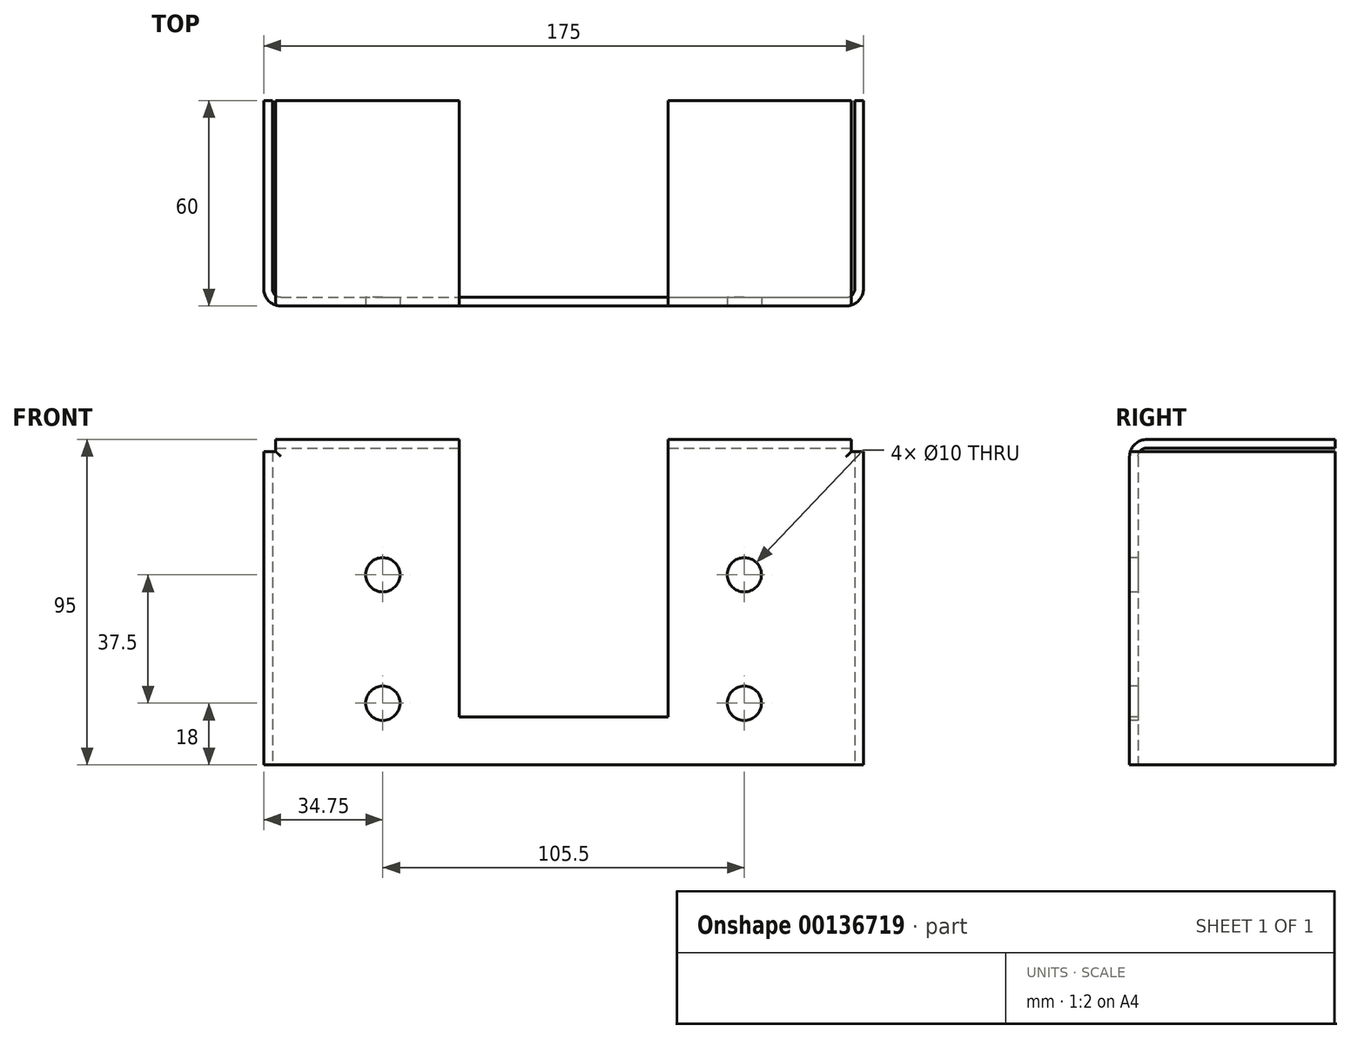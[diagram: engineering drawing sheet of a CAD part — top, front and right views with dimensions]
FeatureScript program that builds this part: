
annotation { "Feature Type Name" : "Feature", "Feature Type Description" : "" }
export const myFeature = defineFeature(function(context is Context, id is Id, definition is map)
    precondition{}
    {
        {
            var Q0;
            Q0=qCreatedBy(makeId("Top.planeOp"),FACE);
            var sketch = newSketch(context, id + "F0", { "sketchPlane" : qUnion([Q0])});
            skLineSegment(sketch, "E0.bottom", {"start": v(-87.5, -30) * mm, "end": v(87.5, -30) * mm});
            skLineSegment(sketch, "E0.top", {"start": v(-87.5, 30) * mm, "end": v(87.5, 30) * mm});
            skLineSegment(sketch, "E0.left", {"start": v(-87.5, -30) * mm, "end": v(-87.5, 30) * mm});
            skLineSegment(sketch, "E0.right", {"start": v(87.5, -30) * mm, "end": v(87.5, 30) * mm});
            skPoint(sketch, "E0.middle", {"position": v(0, 0) * mm});
            skSolve(sketch);
        }
        {
            var Q0;
            Q0 = qSketchRegion(id + "F0", true);
            extrude(context, id + "F1", {"entities" : qUnion([Q0]), "depth" : 95 * mm});
        }
        {
            var Q0;
            Q0=makeQuery(id+"F1.opExtrude","SWEPT_FACE",FACE,{"disambiguationData":[OSD([sQuery(id+"F0.wireOp",EDGE,"E0.bottom")])]});
            var sketch = newSketch(context, id + "F2", { "sketchPlane" : qUnion([Q0])});
            skLineSegment(sketch, "E1", {"start": v(0, 0) * mm, "end": v(0, 95) * mm, "construction": true});
            skPoint(sketch, "E2", {"position": v(0, 14) * mm});
            skLineSegment(sketch, "E3", {"start": v(-30.5, 14) * mm, "end": v(30.5, 14) * mm});
            skLineSegment(sketch, "E4", {"start": v(-30.5, 14) * mm, "end": v(-30.5, 95) * mm});
            skLineSegment(sketch, "E5", {"start": v(-30.5, 95) * mm, "end": v(30.5, 95) * mm});
            skLineSegment(sketch, "E6", {"start": v(30.5, 95) * mm, "end": v(30.5, 14) * mm});
            skSolve(sketch);
        }
        {
            var Q0;
            Q0=makeQuery(id+"F1.opExtrude","SWEPT_FACE",FACE,{"disambiguationData":[OSD([sQuery(id+"F0.wireOp",EDGE,"E0.top")])]});
            var Q1;
            Q1=makeQuery(id+"F1.opExtrude","CAP_FACE",FACE,{"disambiguationData":[OSD([sQuery(id+"F0.wireOp",EDGE,"E0.bottom"),sQuery(id+"F0.wireOp",EDGE,"E0.top"),sQuery(id+"F0.wireOp",EDGE,"E0.left"),sQuery(id+"F0.wireOp",EDGE,"E0.right")])],"isStart":true});
            shell(context, id + "F3", {"entities" : qUnion([Q0, Q1]), "thickness" : 2.5 * mm});
        }
        {
            var Q0;
            Q0 = qSketchRegion(id + "F2", true);
            extrude(context, id + "F4", {"entities" : qUnion([Q0]), "operationType" : NewBodyOperationType.REMOVE, "endBound" : BoundingType.THROUGH_ALL, "oppositeDirection" : true, "depth" : 25 * mm});
        }
        {
            var Q0;
            Q0=makeQuery(id+"F1.opExtrude","SWEPT_FACE",FACE,{"disambiguationData":[OSD([sQuery(id+"F0.wireOp",EDGE,"E0.bottom")])]});
            var sketch = newSketch(context, id + "F5", { "sketchPlane" : qUnion([Q0])});
            skLineSegment(sketch, "E7", {"start": v(0, 36.75) * mm, "end": v(-52.75, 36.75) * mm, "construction": true});
            skLineSegment(sketch, "E8.MirrorCS", {"start": v(0, 36.75) * mm, "end": v(52.75, 36.75) * mm, "construction": true});
            skLineSegment(sketch, "E9.bottom", {"start": v(-52.75, 18) * mm, "end": v(52.75, 18) * mm, "construction": true});
            skLineSegment(sketch, "E9.top", {"start": v(-52.75, 55.5) * mm, "end": v(52.75, 55.5) * mm, "construction": true});
            skLineSegment(sketch, "E9.left", {"start": v(-52.75, 18) * mm, "end": v(-52.75, 55.5) * mm, "construction": true});
            skLineSegment(sketch, "E9.right", {"start": v(52.75, 18) * mm, "end": v(52.75, 55.5) * mm, "construction": true});
            skPoint(sketch, "E9.middle", {"position": v(0, 36.75) * mm});
            skLineSegment(sketch, "E10", {"start": v(0, 18) * mm, "end": v(0, 55.5) * mm, "construction": true});
            skCircle(sketch, "E11", {"center": v(52.75, 55.5) * mm, "radius": 11.25 * mm});
            skCircle(sketch, "E12.MirrorC", {"center": v(52.75, 18) * mm, "radius": 11.25 * mm});
            skCircle(sketch, "E13.MirrorC", {"center": v(-52.75, 18) * mm, "radius": 11.25 * mm});
            skCircle(sketch, "E14.MirrorC", {"center": v(-52.75, 55.5) * mm, "radius": 11.25 * mm});
            skCircle(sketch, "E15", {"center": v(52.75, 55.5) * mm, "radius": 9.15 * mm});
            skCircle(sketch, "E16.MirrorC", {"center": v(52.75, 18) * mm, "radius": 9.15 * mm});
            skCircle(sketch, "E17.MirrorC", {"center": v(-52.75, 55.5) * mm, "radius": 9.15 * mm});
            skCircle(sketch, "E18.MirrorC", {"center": v(-52.75, 18) * mm, "radius": 9.15 * mm});
            skSolve(sketch);
        }
        {
            var Q0;
            Q0=sQuery(id+"F5.wireOp",VERTEX,"E9.right.end");
            var Q1;
            Q1=sQuery(id+"F5.wireOp",VERTEX,"E12.MirrorC.center");
            var Q2;
            Q2=sQuery(id+"F5.wireOp",VERTEX,"E9.left.start");
            var Q3;
            Q3=sQuery(id+"F5.wireOp",VERTEX,"E9.left.end");
            var Q4;
            Q4=makeQuery(id+"F1.opExtrude","SWEPT_BODY",BODY,{"disambiguationData":[OSD([sQuery(id+"F0.wireOp",EDGE,"E0.bottom"),sQuery(id+"F0.wireOp",EDGE,"E0.top"),sQuery(id+"F0.wireOp",EDGE,"E0.left"),sQuery(id+"F0.wireOp",EDGE,"E0.right")])]});
            hole(context, id + "F6", {"style" : HoleStyle.SIMPLE, "endStyle" : HoleEndStyle.THROUGH, "holeDiameter" : 10 * mm, "locations" : qUnion([Q0, Q1, Q2, Q3]), "scope" : qUnion([Q4]), "isTappedThrough" : true});
        }
        {
            var Q0;
            Q0=makeQuery(id+"F1.opExtrude","SWEPT_FACE",FACE,{"disambiguationData":[OSD([sQuery(id+"F0.wireOp",EDGE,"E0.bottom")])]});
            var sketch = newSketch(context, id + "F7", { "sketchPlane" : qUnion([Q0])});
            skLineSegment(sketch, "E19.bottom", {"start": v(-87.5, 95) * mm, "end": v(-84, 95) * mm});
            skLineSegment(sketch, "E19.top", {"start": v(-87.5, 91.5) * mm, "end": v(-84, 91.5) * mm});
            skLineSegment(sketch, "E19.left", {"start": v(-87.5, 95) * mm, "end": v(-87.5, 91.5) * mm});
            skLineSegment(sketch, "E19.right", {"start": v(-84, 95) * mm, "end": v(-84, 91.5) * mm});
            skLineSegment(sketch, "E20", {"start": v(0, 14) * mm, "end": v(0, 97.66) * mm, "construction": true});
            skPoint(sketch, "E20.endSnap0", {"position": v(0, 14) * mm});
            skLineSegment(sketch, "E21.MirrorCS", {"start": v(87.5, 91.5) * mm, "end": v(84, 91.5) * mm});
            skLineSegment(sketch, "E22.MirrorCS", {"start": v(84, 95) * mm, "end": v(84, 91.5) * mm});
            skLineSegment(sketch, "E23.MirrorCS", {"start": v(87.5, 95) * mm, "end": v(84, 95) * mm});
            skLineSegment(sketch, "E24.MirrorCS", {"start": v(87.5, 95) * mm, "end": v(87.5, 91.5) * mm});
            skSolve(sketch);
        }
        {
            var Q0;
            Q0 = qSketchRegion(id + "F7", true);
            extrude(context, id + "F8", {"entities" : qUnion([Q0]), "operationType" : NewBodyOperationType.REMOVE, "endBound" : BoundingType.THROUGH_ALL, "oppositeDirection" : true, "depth" : 25 * mm});
        }
        {
            var Q0;
            Q0=makeQuery(id+"F1.opExtrude","SWEPT_EDGE",EDGE,{"disambiguationData":[OSD([sQuery(id+"F0.wireOp",EDGE,"E0.bottom"),sQuery(id+"F0.wireOp",EDGE,"E0.left")])]});
            var Q1;
            Q1=makeQuery(id+"F1.opExtrude","SWEPT_EDGE",EDGE,{"disambiguationData":[OSD([sQuery(id+"F0.wireOp",EDGE,"E0.bottom"),sQuery(id+"F0.wireOp",EDGE,"E0.right")])]});
            var Q2;
            {var subQ0=sQuery(id+"F0.wireOp",EDGE,"E0.bottom");var subQ1=sQuery(id+"F0.wireOp",EDGE,"E0.left");Q2=makeQuery(id+"F4.boolean.opBoolean","SPLIT",EDGE,{"disambiguationData":[TD([makeQuery(id+"F1.opExtrude","SWEPT_FACE",FACE,{"disambiguationData":[OSD([subQ1])]})])],"derivedFrom":makeQuery(id+"F1.opExtrude","CAP_EDGE",EDGE,{"disambiguationData":[OSD([subQ0])],"isStart":false})});}
            var Q3;
            {var subQ0=sQuery(id+"F0.wireOp",EDGE,"E0.bottom");var subQ1=sQuery(id+"F0.wireOp",EDGE,"E0.right");Q3=makeQuery(id+"F4.boolean.opBoolean","SPLIT",EDGE,{"disambiguationData":[TD([makeQuery(id+"F1.opExtrude","SWEPT_FACE",FACE,{"disambiguationData":[OSD([subQ1])]})])],"derivedFrom":makeQuery(id+"F1.opExtrude","CAP_EDGE",EDGE,{"disambiguationData":[OSD([subQ0])],"isStart":false})});}
            fillet(context, id + "F9", {"entities" : qUnion([Q0, Q1, Q2, Q3]), "radius" : 5 * mm, "tangentPropagation" : true, "allowEdgeOverflow" : false});
        }
        {
            var Q0;
            {var subQ0=sQuery(id+"F0.wireOp",EDGE,"E0.bottom");var subQ1=sQuery(id+"F0.wireOp",EDGE,"E0.right");Q0=makeQuery(id+"F4.boolean.opBoolean","SPLIT",EDGE,{"disambiguationData":[TD([makeQuery(id+"F3.opShell","OFFSET_FACE",FACE,{"disambiguationData":[OSD([subQ1])]})])],"derivedFrom":makeQuery(id+"F3.opShell","OFFSET_EDGE",EDGE,{"disambiguationData":[OSD([subQ0]),TDD([makeQuery(id+"F1.opExtrude","CAP_EDGE",EDGE,{"disambiguationData":[OSD([subQ0])],"isStart":false})])]})});}
            fillet(context, id + "F10", {"entities" : qUnion([Q0]), "radius" : 2.5 * mm, "tangentPropagation" : true, "allowEdgeOverflow" : false});
        }
        {
            var Q0;
            Q0=makeQuery(id+"F3.opShell","OFFSET_EDGE",EDGE,{"disambiguationData":[OSD([sQuery(id+"F0.wireOp",EDGE,"E0.bottom"),sQuery(id+"F0.wireOp",EDGE,"E0.right")])]});
            fillet(context, id + "F11", {"entities" : qUnion([Q0]), "radius" : 2.5 * mm, "tangentPropagation" : true, "allowEdgeOverflow" : false});
        }
        {
            var Q0;
            {var subQ0=sQuery(id+"F0.wireOp",EDGE,"E0.bottom");var subQ1=sQuery(id+"F0.wireOp",EDGE,"E0.left");Q0=makeQuery(id+"F4.boolean.opBoolean","SPLIT",EDGE,{"disambiguationData":[TD([makeQuery(id+"F3.opShell","OFFSET_FACE",FACE,{"disambiguationData":[OSD([subQ1])]})])],"derivedFrom":makeQuery(id+"F3.opShell","OFFSET_EDGE",EDGE,{"disambiguationData":[OSD([subQ0]),TDD([makeQuery(id+"F1.opExtrude","CAP_EDGE",EDGE,{"disambiguationData":[OSD([subQ0])],"isStart":false})])]})});}
            fillet(context, id + "F12", {"entities" : qUnion([Q0]), "radius" : 2.5 * mm, "tangentPropagation" : true, "allowEdgeOverflow" : false});
        }
        {
            var Q0;
            Q0=makeQuery(id+"F3.opShell","OFFSET_EDGE",EDGE,{"disambiguationData":[OSD([sQuery(id+"F0.wireOp",EDGE,"E0.bottom"),sQuery(id+"F0.wireOp",EDGE,"E0.left")])]});
            fillet(context, id + "F13", {"entities" : qUnion([Q0]), "radius" : 2.5 * mm, "tangentPropagation" : true, "allowEdgeOverflow" : false});
        }
    });
